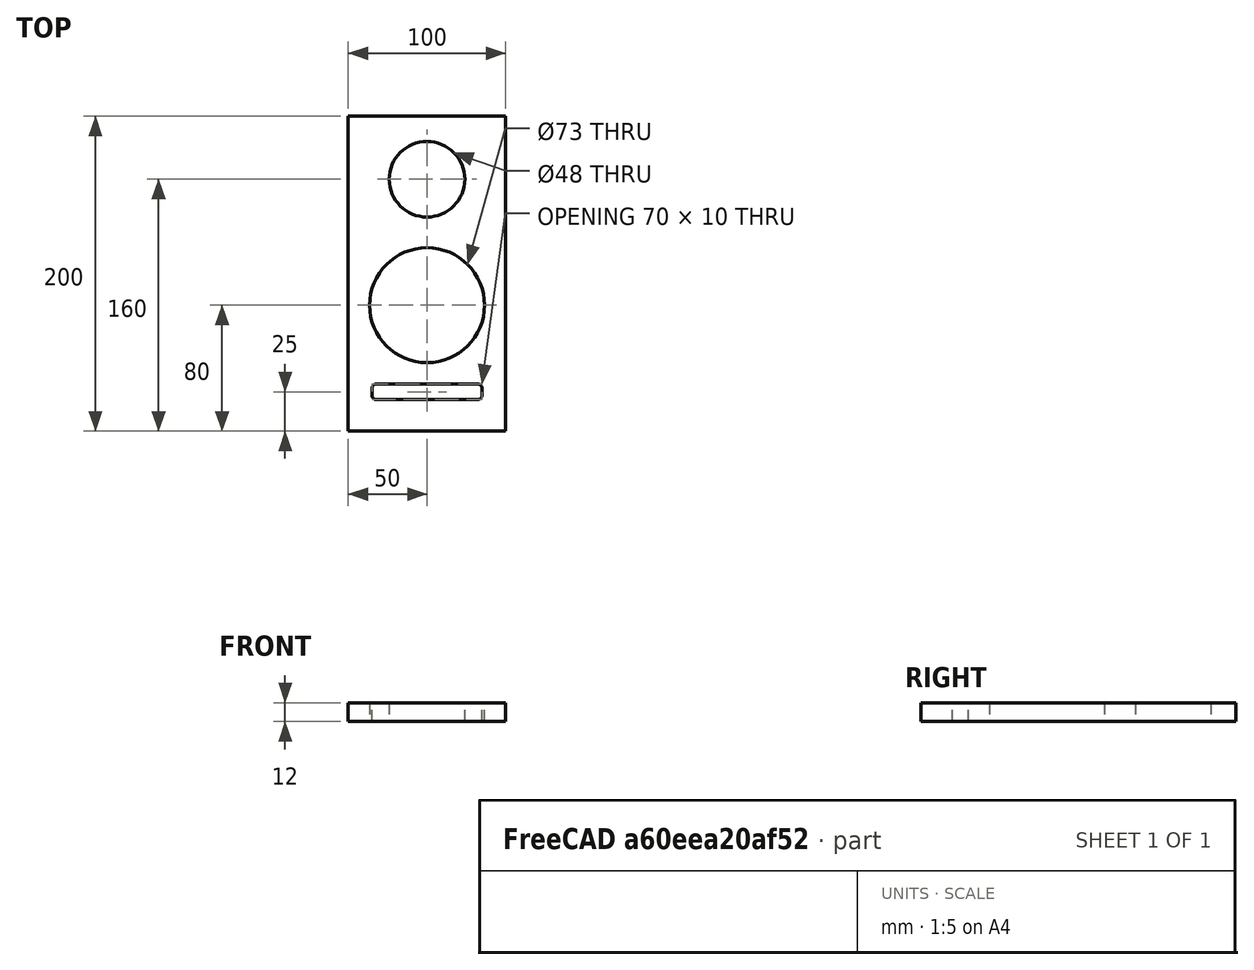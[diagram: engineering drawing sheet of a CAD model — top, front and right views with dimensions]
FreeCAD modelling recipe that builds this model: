
FCSTD DOCUMENT  (FreeCAD 0.16R6703 (Git))
Label: box2_front_2way
License: All rights reserved
LicenseURL: http://en.wikipedia.org/wiki/All_rights_reserved
objects: Sketcher::SketchObject×1, PartDesign::Pad×1
note: 3 computed .brp shape members not serialized (recipe doc carries the construction recipe); baked Part::Feature solids carry a one-line shape summary decoded from their .brp

FEATURE [Sketcher::SketchObject] Sketch
  expr: Constraints[16] = 73 / 2
  sketch-geometry (16):
    g0: LineSegment StartX=0 StartY=0 StartZ=0 EndX=100 EndY=0 EndZ=0
    g1: LineSegment StartX=100 StartY=0 StartZ=0 EndX=100 EndY=200 EndZ=0
    g2: LineSegment StartX=100 StartY=200 StartZ=0 EndX=0 EndY=200 EndZ=0
    g3: LineSegment StartX=0 StartY=200 StartZ=0 EndX=0 EndY=0 EndZ=0
    g4: LineSegment [constr] StartX=0 StartY=80 StartZ=0 EndX=100 EndY=80 EndZ=0
    g5: Circle CenterX=50 CenterY=80 CenterZ=0 NormalX=0 NormalY=0 NormalZ=1 Radius=36.5
    g6: LineSegment StartX=18 StartY=20 StartZ=0 EndX=82 EndY=20 EndZ=0
    g7: LineSegment StartX=85 StartY=23 StartZ=0 EndX=85 EndY=27 EndZ=0
    g8: LineSegment StartX=82 StartY=30 StartZ=0 EndX=18 EndY=30 EndZ=0
    g9: LineSegment StartX=15 StartY=27 StartZ=0 EndX=15 EndY=23 EndZ=0
    g10: ArcOfCircle CenterX=18 CenterY=27 CenterZ=0 NormalX=0 NormalY=0 NormalZ=1 Radius=3 StartAngle=1.5708 EndAngle=3.14159
    g11: ArcOfCircle CenterX=18 CenterY=23 CenterZ=0 NormalX=0 NormalY=0 NormalZ=1 Radius=3 StartAngle=3.14159 EndAngle=4.71239
    g12: ArcOfCircle CenterX=82 CenterY=23 CenterZ=0 NormalX=0 NormalY=0 NormalZ=1 Radius=3 StartAngle=4.71239 EndAngle=6.28319
    g13: ArcOfCircle CenterX=82 CenterY=27 CenterZ=0 NormalX=0 NormalY=0 NormalZ=1 Radius=3 StartAngle=0 EndAngle=1.5708
    g14: LineSegment [constr] StartX=0 StartY=160 StartZ=0 EndX=100 EndY=160 EndZ=0
    g15: Circle CenterX=50 CenterY=160 CenterZ=0 NormalX=0 NormalY=0 NormalZ=1 Radius=24
  constraints (45):
    c: Coincident(g0,g1)
    c: Coincident(g1,g2)
    c: Coincident(g2,g3)
    c: Coincident(g3,g0)
    c: Horizontal(g0)
    c: Horizontal(g2)
    c: Vertical(g1)
    c: Vertical(g3)
    c: Coincident(g0,g-1)
    c: Distance(g1) = 200
    c: Distance(g0) = 100
    c: PointOnObject(g4,g3)
    c: PointOnObject(g4,g1)
    c: Horizontal(g4)
    c: PointOnObject(g5,g4)
    c: Symmetric(g4,g4,g5)
    c: Radius(g5) = 36.5
    c: DistanceY(g4,g2) = 120
    c: Horizontal(g6)
    c: Horizontal(g8)
    c: Vertical(g7)
    c: Vertical(g9)
    c: Tangent(g8,g10) = -1.5708
    c: Tangent(g9,g10) = -1.5708
    c: Tangent(g6,g11) = -1.5708
    c: Tangent(g9,g11) = -1.5708
    c: Tangent(g6,g12) = -1.5708
    c: Tangent(g7,g12) = -1.5708
    c: Tangent(g7,g13) = -1.5708
    c: Tangent(g8,g13) = -1.5708
    c: DistanceY(g6,g8) = 10
    c: DistanceX(g-1,g9) = 15
    c: DistanceX(g7,g0) = 15
    c: DistanceX(g11,g10) = 0
    c: DistanceX(g12,g13) = 0
    c: DistanceY(g-1,g6) = 20
    c: Equal(g10,g13)
    c: Radius(g13) = 3
    c: PointOnObject(g14,g3)
    c: PointOnObject(g14,g1)
    c: Horizontal(g14)
    c: PointOnObject(g15,g14)
    c: Symmetric(g14,g14,g15)
    c: DistanceY(g14,g1) = 40
    c: Radius(g15) = 24
FEATURE [PartDesign::Pad] Pad
  Length = 12
  Length2 = 100
  Sketch = -> Sketch
  Type = 0
